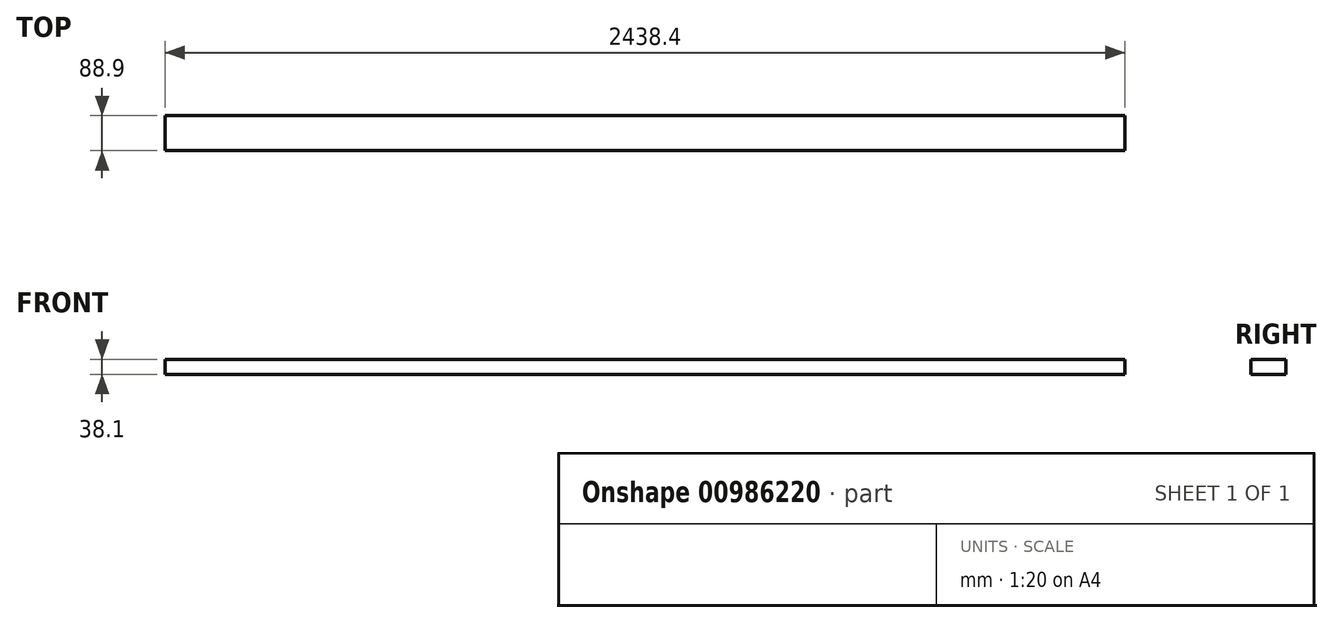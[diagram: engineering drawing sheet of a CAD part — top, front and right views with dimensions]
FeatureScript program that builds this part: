
annotation { "Feature Type Name" : "Feature", "Feature Type Description" : "" }
export const myFeature = defineFeature(function(context is Context, id is Id, definition is map)
    precondition{}
    {
        {
            var Q0;
            Q0=qCreatedBy(makeId("Right.planeOp"),FACE);
            var sketch = newSketch(context, id + "F0", { "sketchPlane" : qUnion([Q0])});
            skLineSegment(sketch, "E0.bottom", {"start": v(-44.45, 19.05) * mm, "end": v(44.45, 19.05) * mm});
            skLineSegment(sketch, "E0.top", {"start": v(-44.45, -19.05) * mm, "end": v(44.45, -19.05) * mm});
            skLineSegment(sketch, "E0.left", {"start": v(-44.45, 19.05) * mm, "end": v(-44.45, -19.05) * mm});
            skLineSegment(sketch, "E0.right", {"start": v(44.45, 19.05) * mm, "end": v(44.45, -19.05) * mm});
            skPoint(sketch, "E0.middle", {"position": v(0, 0) * mm});
            skSolve(sketch);
        }
        {
            var Q0;
            Q0=makeQuery(id+"F0.imprint","IMPRINT",FACE,{"disambiguationData":[TD([[makeQuery(id+"F0.imprint","IMPRINT",EDGE,{"derivedFrom":sQuery(id+"F0.wireOp",EDGE,"E0.bottom")}),-1.0]])]});
            extrude(context, id + "F1", {"entities" : qUnion([Q0]), "depth" : 2438.4 * mm, "offsetDistance" : 25.4 * mm});
        }
    });
